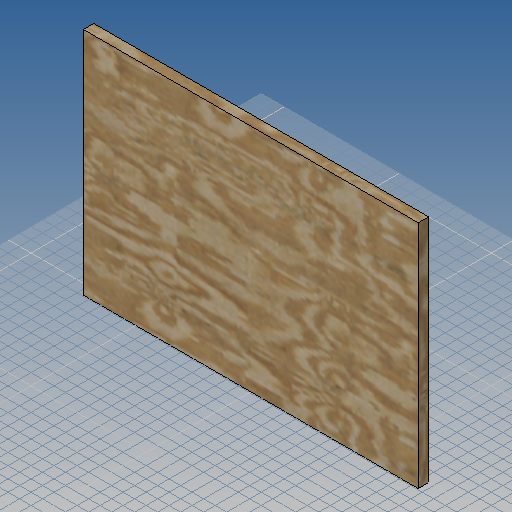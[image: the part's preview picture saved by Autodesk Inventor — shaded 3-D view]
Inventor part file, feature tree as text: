
AUTODESK INVENTOR PART (.ipt)
format: ipt  version: 2019 (Build 230136000, 136)  size: 311,296 bytes
history: native  units: mm
features: other x1, extrude x1, sketch x1
ambient origin geometry x8: Origin, YZ Plane, XZ Plane, XY Plane, X Axis, Y Axis, Z Axis, Center Point
bodies: Volumenkörper1 (feature_tree)
feature tree (3):
  other  "<userpath>\OneDrive\Dokumente\Inventor\Absauganlage\Absauganlage_Params.xlsx"
  extrude  "Extrusion1"  Depth=400.0mm
  sketch  "Skizze1"  dims[d0=582.0mm d1=400.0mm d2=18.0mm d3=0.0mm]
